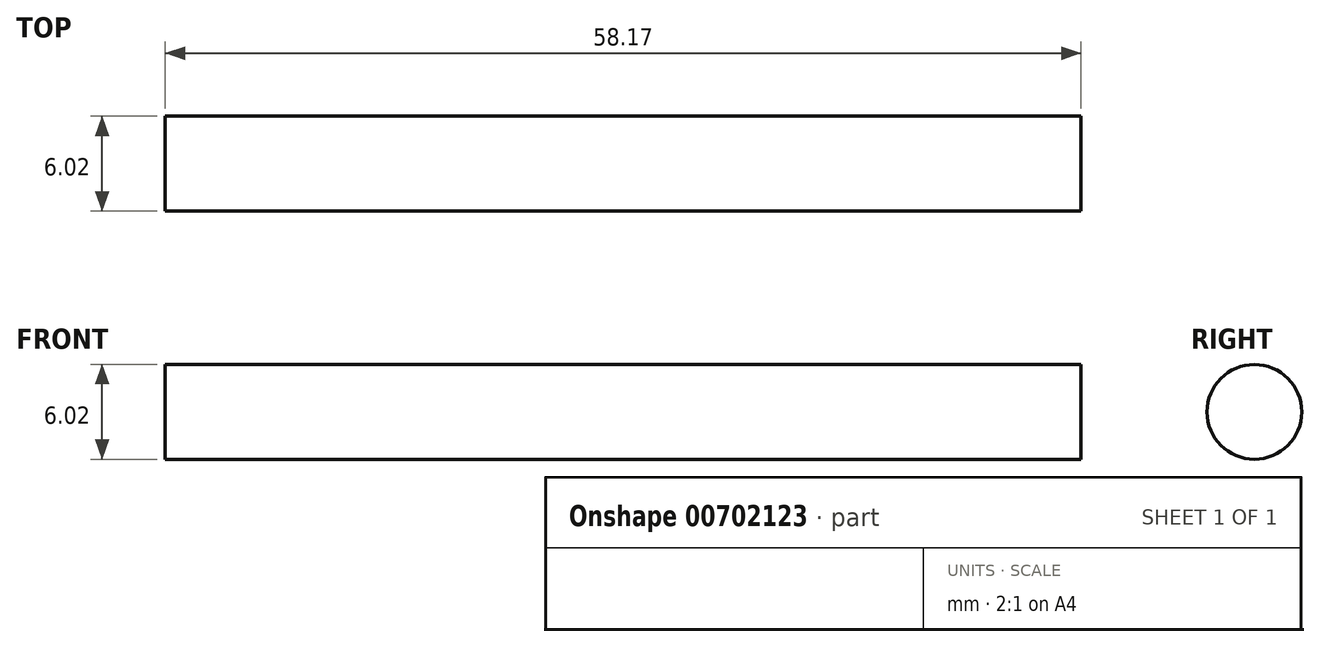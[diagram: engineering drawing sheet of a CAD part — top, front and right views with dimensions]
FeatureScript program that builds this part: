
annotation { "Feature Type Name" : "Feature", "Feature Type Description" : "" }
export const myFeature = defineFeature(function(context is Context, id is Id, definition is map)
    precondition{}
    {
        {
            var Q0;
            Q0=qCreatedBy(makeId("Right.planeOp"),FACE);
            var sketch = newSketch(context, id + "F0", { "sketchPlane" : qUnion([Q0])});
            skCircle(sketch, "E0", {"center": v(0, 0) * mm, "radius": 3.01 * mm});
            skSolve(sketch);
        }
        {
            var Q0;
            Q0 = qSketchRegion(id + "F0", true);
            extrude(context, id + "F1", {"entities" : qUnion([Q0]), "depth" : 58.17 * mm, "offsetDistance" : 25.4 * mm});
        }
    });
